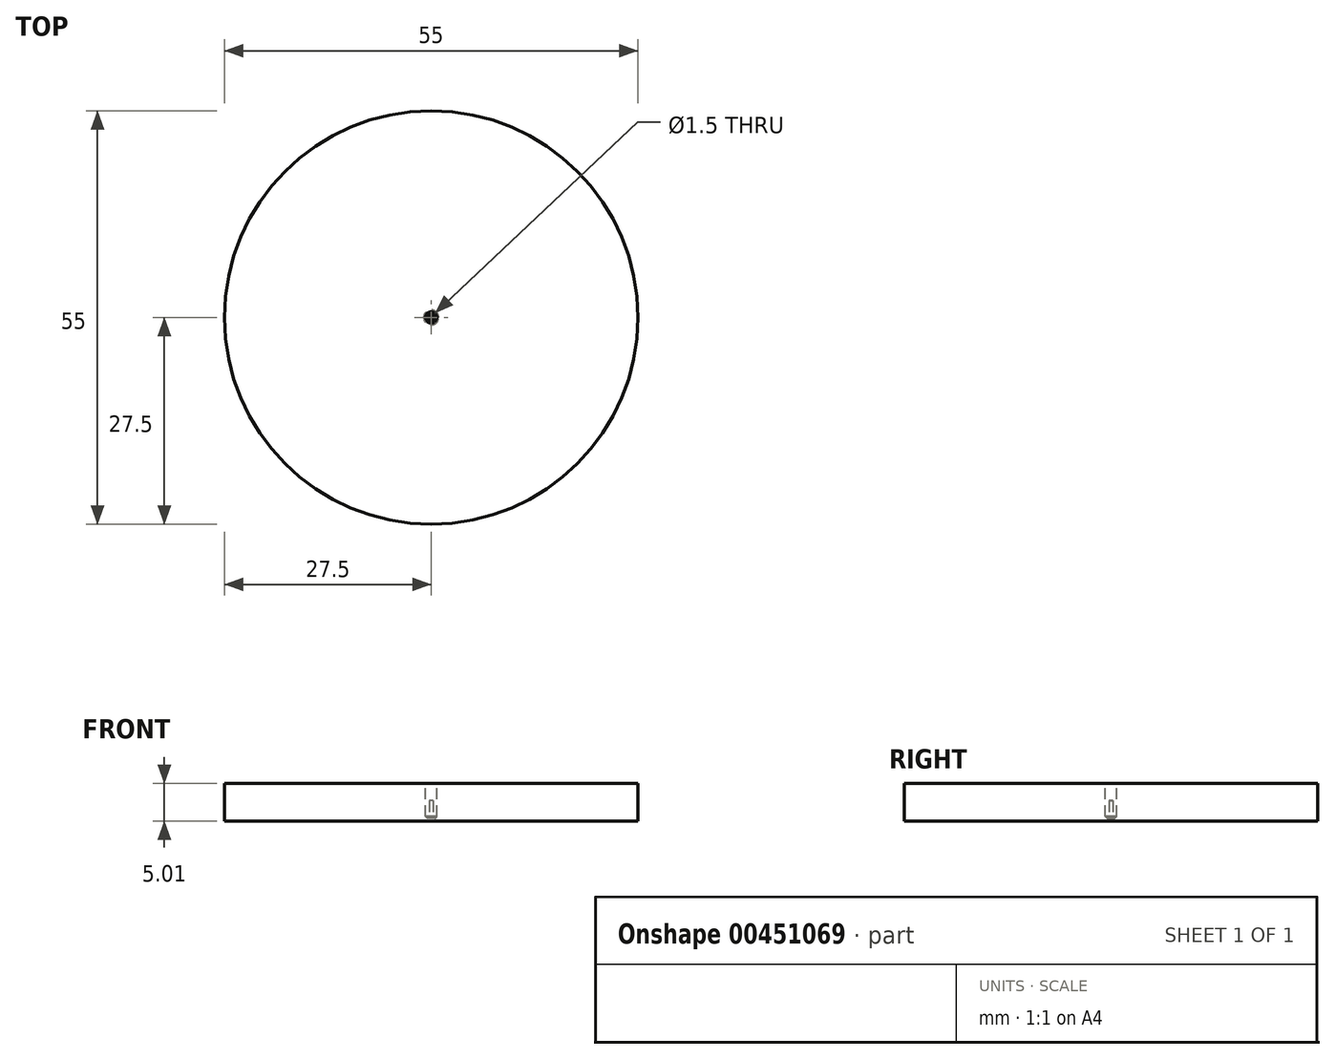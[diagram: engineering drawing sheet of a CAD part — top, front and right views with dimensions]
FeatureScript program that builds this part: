
annotation { "Feature Type Name" : "Feature", "Feature Type Description" : "" }
export const myFeature = defineFeature(function(context is Context, id is Id, definition is map)
    precondition{}
    {
        {
            var Q0;
            Q0=qCreatedBy(makeId("Top.planeOp"),FACE);
            var sketch = newSketch(context, id + "F0", { "sketchPlane" : qUnion([Q0])});
            skCircle(sketch, "E0", {"center": v(0, 0) * mm, "radius": 27.5 * mm});
            skSolve(sketch);
        }
        {
            var Q0;
            Q0=makeQuery(id+"F0.imprint","IMPRINT",FACE,{"disambiguationData":[TD([[makeQuery(id+"F0.imprint","IMPRINT",EDGE,{"derivedFrom":sQuery(id+"F0.wireOp",EDGE,"E0")}),1.0]])]});
            extrude(context, id + "F1", {"entities" : qUnion([Q0]), "depth" : 5 * mm});
        }
        {
            var Q0;
            Q0=makeQuery(id+"F1.opExtrude","CAP_FACE",FACE,{"disambiguationData":[OSD([sQuery(id+"F0.wireOp",EDGE,"E0")])],"isStart":false});
            var sketch = newSketch(context, id + "F2", { "sketchPlane" : qUnion([Q0])});
            skCircle(sketch, "E1", {"center": v(0, 0) * mm, "radius": 0.75 * mm});
            skSolve(sketch);
        }
        {
            var Q0;
            Q0=qSketchRegion(id+"F2",true);
            extrude(context, id + "F3", {"entities" : qUnion([Q0]), "operationType" : NewBodyOperationType.REMOVE, "oppositeDirection" : true, "depth" : 4.65 * mm});
        }
        {
            var Q0;
            Q0=makeQuery(id+"F3.boolean.opBoolean","COPY",FACE,{"derivedFrom":makeQuery(id+"F3.opExtrude","CAP_FACE",FACE,{"disambiguationData":[OSD([sQuery(id+"F2.wireOp",EDGE,"E1")])],"isStart":false})});
            var sketch = newSketch(context, id + "F4", { "sketchPlane" : qUnion([Q0])});
            skCircle(sketch, "E2", {"center": v(0, 0) * mm, "radius": 0.25 * mm});
            skSolve(sketch);
        }
        {
            var Q0;
            Q0=qSketchRegion(id+"F4",true);
            extrude(context, id + "F5", {"entities" : qUnion([Q0]), "operationType" : NewBodyOperationType.ADD, "depth" : 2.35 * mm});
        }
        {
            var Q0;
            Q0=makeQuery(id+"F3.boolean.opBoolean","COPY",EDGE,{"derivedFrom":makeQuery(id+"F3.opExtrude","CAP_EDGE",EDGE,{"disambiguationData":[OSD([sQuery(id+"F2.wireOp",EDGE,"E1")])],"isStart":false})});
            chamfer(context, id + "F6", {"entities" : qUnion([Q0]), "width" : 0.25 * mm, "tangentPropagation" : true});
        }
        {
            var Q0;
            Q0=makeQuery(id+"F1.opExtrude","CAP_FACE",FACE,{"disambiguationData":[OSD([sQuery(id+"F0.wireOp",EDGE,"E0")])],"isStart":true});
            var sketch = newSketch(context, id + "F7", { "sketchPlane" : qUnion([Q0])});
            skCircle(sketch, "E3", {"center": v(0, 0) * mm, "radius": 1 * mm});
            skSolve(sketch);
        }
        {
            var Q0;
            Q0=qSketchRegion(id+"F7",true);
            extrude(context, id + "F8", {"entities" : qUnion([Q0]), "operationType" : NewBodyOperationType.ADD, "depth" : 0.01 * mm});
        }
    });
